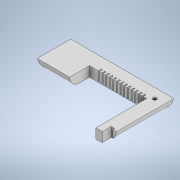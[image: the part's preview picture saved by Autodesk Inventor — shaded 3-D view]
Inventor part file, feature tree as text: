
AUTODESK INVENTOR PART (.ipt)
format: ipt  version: 2020 (Build 240168000, 168)  size: 1,034,752 bytes
history: native  units: mm
features: other x3, sketch x2, extrude x1
ambient origin geometry x8: Origin, YZ Plane, XZ Plane, XY Plane, X Axis, Y Axis, Z Axis, Center Point
bodies: Solid1 (feature_tree)
feature tree (6):
  other  "casing-backing.ipt"
  extrude  "Extrusion1"  TaperAngle=0.0deg  [1 undecoded]
  other  "Solid4::casing-backing.ipt"
  other  "TaggingFeature1"
  sketch  "Sketch1"  dims[d0=10.0mm d1=0.0mm d2=0.0mm]
  sketch  "Sketch6"
note: 1 required parameter value undecoded (feature->parameter linkage not recoverable at this tier; creation-order binding heuristic only, values carry confidence <= 0.55)
